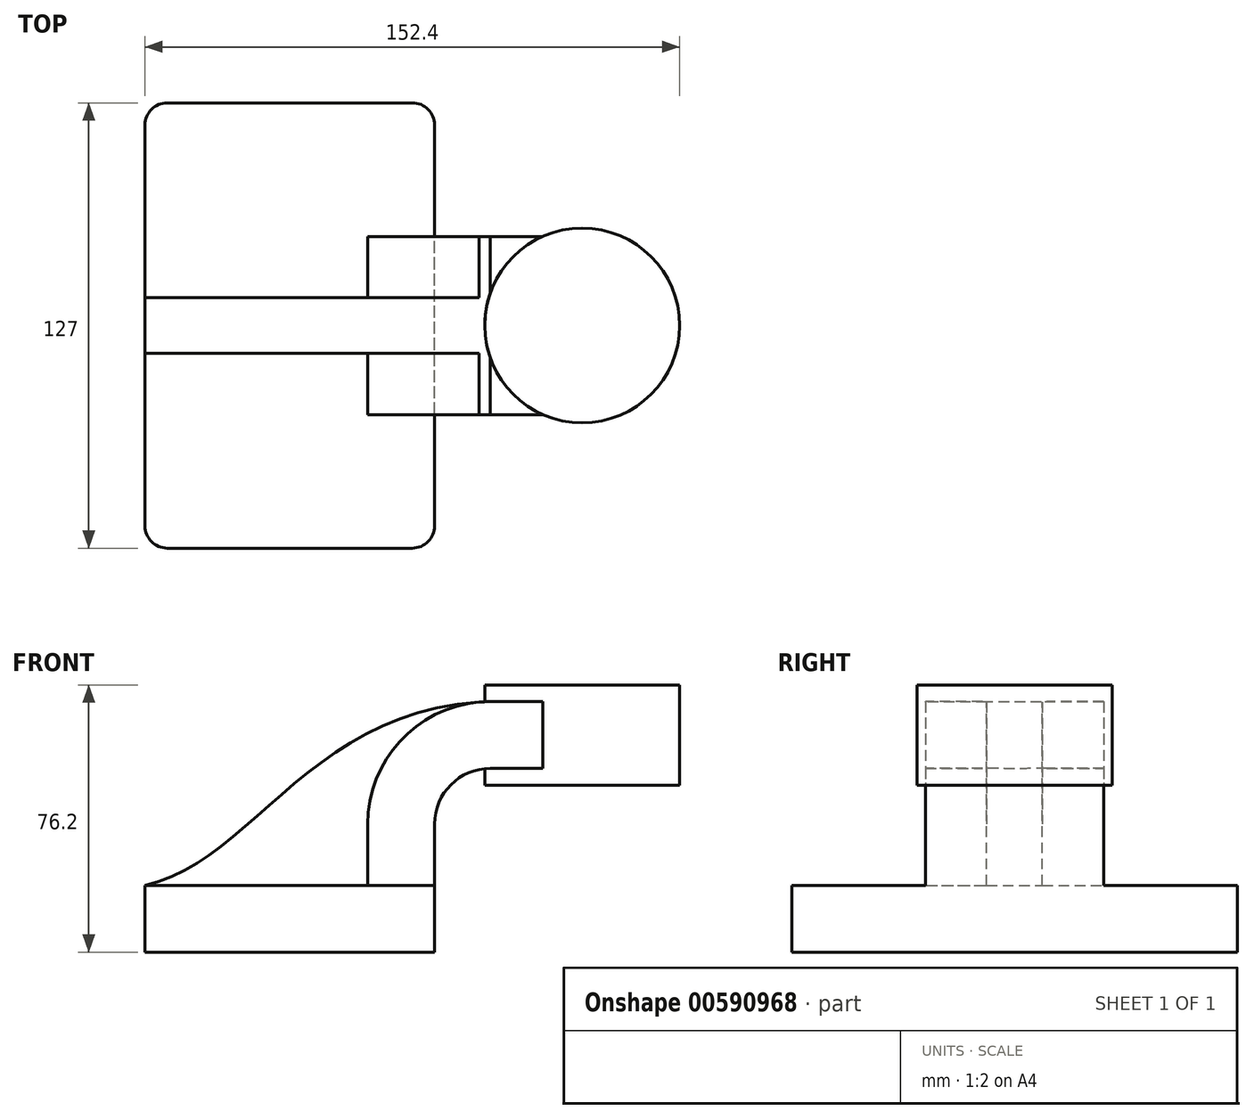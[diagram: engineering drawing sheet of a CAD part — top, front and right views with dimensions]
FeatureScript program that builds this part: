
annotation { "Feature Type Name" : "Feature", "Feature Type Description" : "" }
export const myFeature = defineFeature(function(context is Context, id is Id, definition is map)
    precondition{}
    {
        {
            var Q0;
            Q0=qCreatedBy(makeId("Front.planeOp"),FACE);
            var sketch = newSketch(context, id + "F0", { "sketchPlane" : qUnion([Q0])});
            skLineSegment(sketch, "E0.bottom", {"start": v(37.08, 1.28) * mm, "end": v(-45.47, 1.28) * mm});
            skLineSegment(sketch, "E0.top", {"start": v(37.08, -17.77) * mm, "end": v(-45.47, -17.77) * mm});
            skLineSegment(sketch, "E0.left", {"start": v(37.08, 1.28) * mm, "end": v(37.08, -17.77) * mm});
            skLineSegment(sketch, "E0.right", {"start": v(-45.47, 1.28) * mm, "end": v(-45.47, -17.77) * mm});
            skLineSegment(sketch, "E1.bottom", {"start": v(106.93, 58.43) * mm, "end": v(56.13, 58.43) * mm});
            skLineSegment(sketch, "E1.top", {"start": v(106.93, 29.85) * mm, "end": v(56.13, 29.85) * mm});
            skLineSegment(sketch, "E1.left", {"start": v(106.93, 58.43) * mm, "end": v(106.93, 29.85) * mm});
            skLineSegment(sketch, "E1.right", {"start": v(56.13, 58.43) * mm, "end": v(56.13, 29.85) * mm});
            skPoint(sketch, "E1.middle", {"position": v(81.53, 44.14) * mm});
            skLineSegment(sketch, "E2", {"start": v(52.96, 34.63) * mm, "end": v(79.17, 34.63) * mm});
            skLineSegment(sketch, "E3", {"start": v(37.08, 1.28) * mm, "end": v(37.08, 18.75) * mm});
            skArc(sketch, "E4", {"start": v(37.08, 18.75) * mm, "mid": v(41.73, 29.98) * mm, "end": v(52.96, 34.63) * mm});
            skLineSegment(sketch, "E5.0", {"start": v(52.96, 53.68) * mm, "end": v(79.17, 53.68) * mm});
            skArc(sketch, "E5.1", {"start": v(18.03, 18.75) * mm, "mid": v(28.26, 43.45) * mm, "end": v(52.96, 53.68) * mm});
            skLineSegment(sketch, "E5.2", {"start": v(18.03, 1.28) * mm, "end": v(18.03, 18.75) * mm});
            skLineSegment(sketch, "E6", {"start": v(79.17, 29.85) * mm, "end": v(79.17, 58.43) * mm});
            skFitSpline(sketch, "E7", {"points": [v(-45.47, 1.28) * mm, v(52.96, 53.68) * mm], "startDerivative": vector(93.14, 20.3) * mm, "endDerivative": vector(153.54, 4.19) * mm});
            skSolve(sketch);
        }
        {
            var Q0;
            Q0=makeQuery(id+"F0.imprint","IMPRINT",FACE,{"disambiguationData":[TD([[makeQuery(id+"F0.imprint","IMPRINT",EDGE,{"derivedFrom":sQuery(id+"F0.wireOp",EDGE,"E0.top")}),-1.0]])]});
            extrude(context, id + "F1", {"entities" : qUnion([Q0]), "endBound" : BoundingType.SYMMETRIC, "depth" : 127 * mm, "offsetDistance" : 25.4 * mm});
        }
        {
            var Q0;
            {var subQ6=sQuery(id+"F0.wireOp",EDGE,"E3");Q0=makeQuery(id+"F0.imprint","IMPRINT",FACE,{"disambiguationData":[TD([[makeQuery(id+"F0.imprint","IMPRINT",EDGE,{"derivedFrom":subQ6}),1.0]])]});}
            var Q1;
            {var subQ0=sQuery(id+"F0.wireOp",EDGE,"E5.0");var subQ1=sQuery(id+"F0.wireOp",EDGE,"E1.right");var subQ2=makeQuery(id+"F0.imprint","INTERSECT",VERTEX,{"derivedFrom":[subQ1,subQ0]});Q1=makeQuery(id+"F0.imprint","IMPRINT",FACE,{"disambiguationData":[TD([[makeQuery(id+"F0.imprint","IMPRINT",EDGE,{"disambiguationData":[TD([[subQ2,-1.0]])],"derivedFrom":subQ1}),1.0]])]});}
            extrude(context, id + "F2", {"entities" : qUnion([Q0, Q1]), "operationType" : NewBodyOperationType.ADD, "endBound" : BoundingType.SYMMETRIC, "depth" : 50.8 * mm, "offsetDistance" : 25.4 * mm});
        }
        {
            var Q0;
            {var subQ3=sQuery(id+"F0.wireOp",EDGE,"E5.2");Q0=makeQuery(id+"F0.imprint","IMPRINT",FACE,{"disambiguationData":[TD([[makeQuery(id+"F0.imprint","IMPRINT",EDGE,{"derivedFrom":subQ3}),1.0]])]});}
            extrude(context, id + "F3", {"entities" : qUnion([Q0]), "operationType" : NewBodyOperationType.ADD, "endBound" : BoundingType.SYMMETRIC, "depth" : 15.88 * mm, "offsetDistance" : 25.4 * mm});
        }
        {
            var Q0;
            {var subQ0=sQuery(id+"F0.wireOp",EDGE,"E1.left");Q0=makeQuery(id+"F0.imprint","IMPRINT",FACE,{"disambiguationData":[TD([[makeQuery(id+"F0.imprint","IMPRINT",EDGE,{"derivedFrom":subQ0}),-1.0]])]});}
            var Q1;
            Q1=sQuery(id+"F0.wireOp",EDGE,"E6");
            revolve(context, id + "F4", {"operationType" : NewBodyOperationType.ADD, "entities" : qUnion([Q0]), "axis" : qUnion([Q1]), "revolveType" : RevolveType.FULL});
        }
        {
            var Q0;
            Q0=makeQuery(id+"F1.opExtrude","CAP_EDGE",EDGE,{"disambiguationData":[OSD([sQuery(id+"F0.wireOp",EDGE,"E0.left")])],"isStart":false});
            var Q1;
            Q1=makeQuery(id+"F1.opExtrude","CAP_EDGE",EDGE,{"disambiguationData":[OSD([sQuery(id+"F0.wireOp",EDGE,"E0.right")])],"isStart":false});
            var Q2;
            Q2=makeQuery(id+"F1.opExtrude","CAP_EDGE",EDGE,{"disambiguationData":[OSD([sQuery(id+"F0.wireOp",EDGE,"E0.left")])],"isStart":true});
            var Q3;
            Q3=makeQuery(id+"F1.opExtrude","CAP_EDGE",EDGE,{"disambiguationData":[OSD([sQuery(id+"F0.wireOp",EDGE,"E0.right")])],"isStart":true});
            fillet(context, id + "F5", {"entities" : qUnion([Q0, Q1, Q2, Q3]), "radius" : 6.35 * mm, "tangentPropagation" : true, "allowEdgeOverflow" : false});
        }
    });
